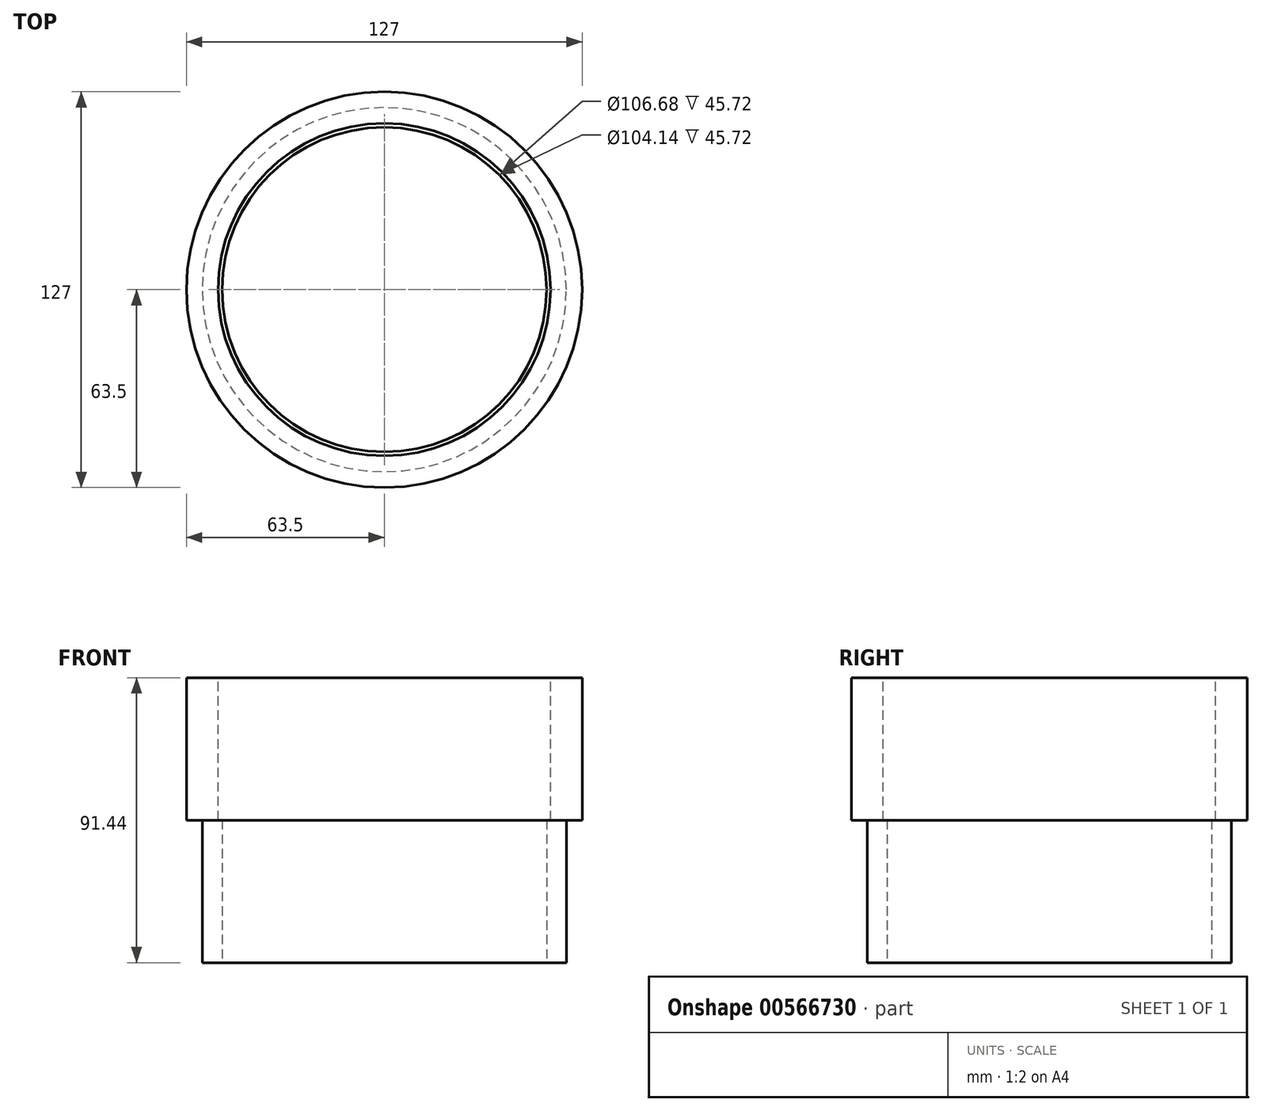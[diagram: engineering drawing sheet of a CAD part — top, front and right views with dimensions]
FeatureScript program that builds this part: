
annotation { "Feature Type Name" : "Feature", "Feature Type Description" : "" }
export const myFeature = defineFeature(function(context is Context, id is Id, definition is map)
    precondition{}
    {
        {
            var Q0;
            Q0=qCreatedBy(makeId("Top.planeOp"),FACE);
            var sketch = newSketch(context, id + "F0", { "sketchPlane" : qUnion([Q0])});
            skCircle(sketch, "E0", {"center": v(0, 0) * mm, "radius": 63.5 * mm});
            skSolve(sketch);
        }
        {
            var Q0;
            Q0=qSketchRegion(id+"F0",true);
            extrude(context, id + "F1", {"entities" : qUnion([Q0]), "depth" : 45.72 * mm, "offsetDistance" : 25.4 * mm});
        }
        {
            var Q0;
            Q0=makeQuery(id+"F1.opExtrude","CAP_FACE",FACE,{"disambiguationData":[OSD([sQuery(id+"F0.wireOp",EDGE,"E0")])],"isStart":false});
            var sketch = newSketch(context, id + "F2", { "sketchPlane" : qUnion([Q0])});
            skCircle(sketch, "E1", {"center": v(0, 0) * mm, "radius": 53.34 * mm});
            skSolve(sketch);
        }
        {
            var Q0;
            Q0=makeQuery(id+"F2.imprint","IMPRINT",FACE,{"disambiguationData":[TD([[makeQuery(id+"F2.imprint","IMPRINT",EDGE,{"derivedFrom":sQuery(id+"F2.wireOp",EDGE,"E1")}),1.0]])]});
            extrude(context, id + "F3", {"entities" : qUnion([Q0]), "operationType" : NewBodyOperationType.REMOVE, "oppositeDirection" : true, "depth" : 50.8 * mm, "offsetDistance" : 25.4 * mm});
        }
        {
            var Q0;
            Q0=qCreatedBy(makeId("Top.planeOp"),FACE);
            var sketch = newSketch(context, id + "F4", { "sketchPlane" : qUnion([Q0])});
            skCircle(sketch, "E2", {"center": v(0, 0) * mm, "radius": 58.42 * mm});
            skSolve(sketch);
        }
        {
            var Q0;
            Q0=qSketchRegion(id+"F4",true);
            extrude(context, id + "F5", {"entities" : qUnion([Q0]), "operationType" : NewBodyOperationType.ADD, "depth" : -45.72 * mm, "offsetDistance" : 25.4 * mm});
        }
        {
            var Q0;
            Q0=makeQuery(id+"F5.opExtrude","CAP_FACE",FACE,{"disambiguationData":[OSD([sQuery(id+"F4.wireOp",EDGE,"E2")])],"isStart":false});
            var sketch = newSketch(context, id + "F6", { "sketchPlane" : qUnion([Q0])});
            skCircle(sketch, "E3", {"center": v(0, 0) * mm, "radius": 52.07 * mm});
            skSolve(sketch);
        }
        {
            var Q0;
            Q0=qSketchRegion(id+"F6",true);
            extrude(context, id + "F7", {"entities" : qUnion([Q0]), "operationType" : NewBodyOperationType.REMOVE, "oppositeDirection" : true, "depth" : 127 * mm, "offsetDistance" : 25.4 * mm});
        }
    });
